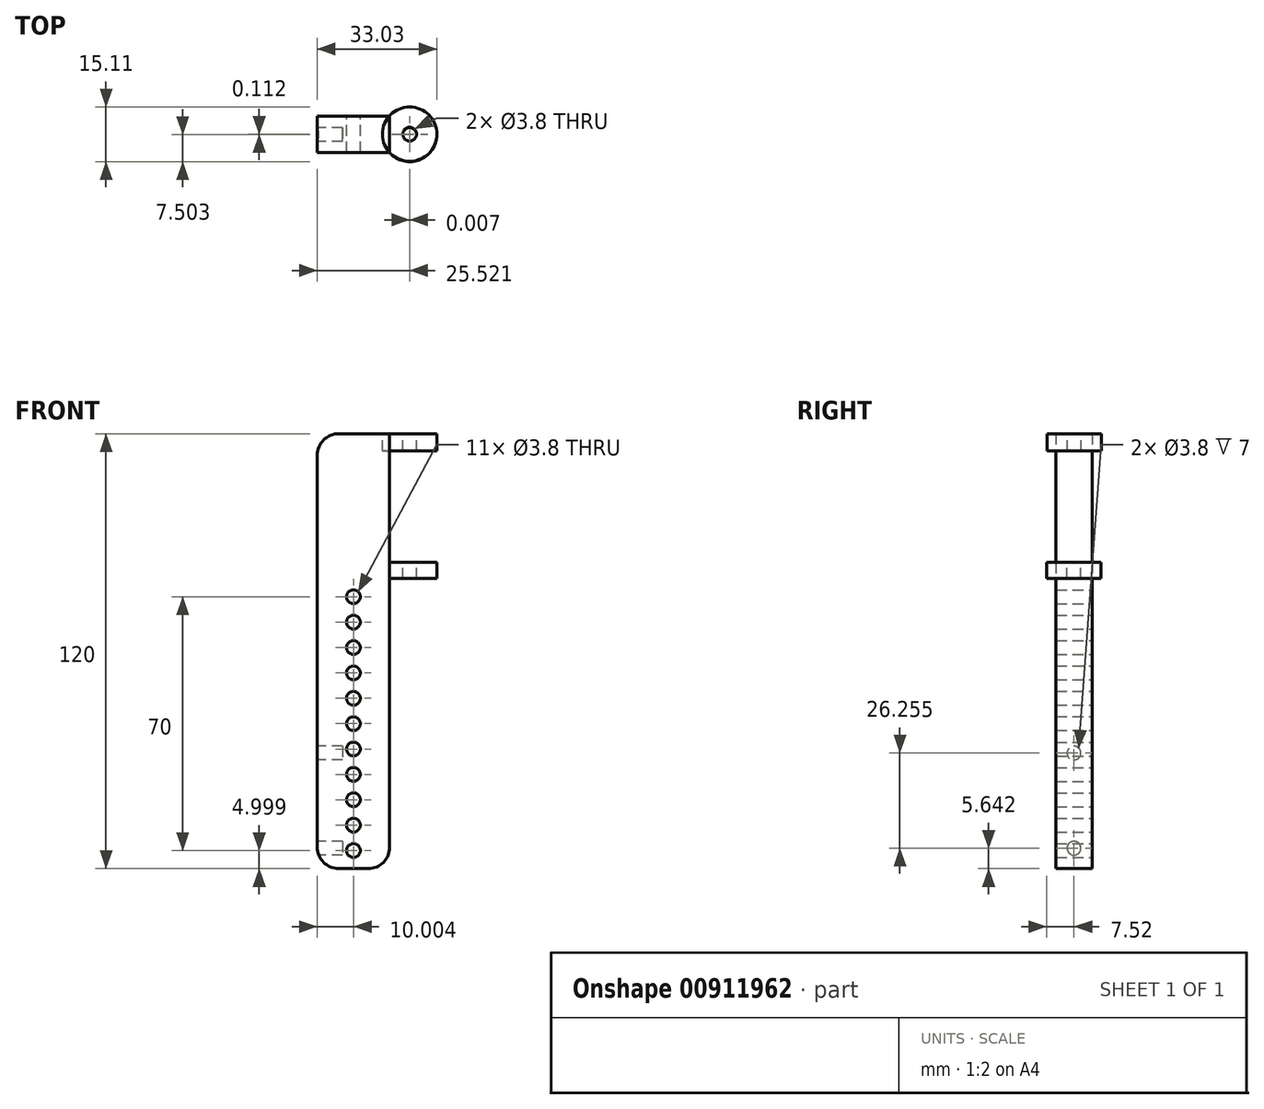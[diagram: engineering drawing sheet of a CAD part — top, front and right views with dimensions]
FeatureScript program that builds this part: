
annotation { "Feature Type Name" : "Feature", "Feature Type Description" : "" }
export const myFeature = defineFeature(function(context is Context, id is Id, definition is map)
    precondition{}
    {
        {
            var Q0;
            Q0=qCreatedBy(makeId("Front.planeOp"),FACE);
            var sketch = newSketch(context, id + "F0", { "sketchPlane" : qUnion([Q0])});
            skLineSegment(sketch, "E0.bottom", {"start": v(-51.22, 126.63) * mm, "end": v(-37.22, 126.63) * mm});
            skLineSegment(sketch, "E0.top", {"start": v(-51.22, 6.63) * mm, "end": v(-43.22, 6.63) * mm});
            skLineSegment(sketch, "E0.left", {"start": v(-57.22, 120.63) * mm, "end": v(-57.22, 12.63) * mm});
            skLineSegment(sketch, "E0.right", {"start": v(-37.22, 126.63) * mm, "end": v(-37.22, 12.63) * mm});
            skPoint(sketch, "E1.visualSharp", {"position": v(-57.22, 126.63) * mm});
            skArc(sketch, "E1.filletArc", {"start": v(-51.22, 126.63) * mm, "mid": v(-55.46, 124.87) * mm, "end": v(-57.22, 120.63) * mm});
            skPoint(sketch, "E2.visualSharp", {"position": v(-57.22, 6.63) * mm});
            skArc(sketch, "E2.filletArc", {"start": v(-57.22, 12.63) * mm, "mid": v(-55.46, 8.39) * mm, "end": v(-51.22, 6.63) * mm});
            skPoint(sketch, "E3.visualSharp", {"position": v(-37.22, 6.63) * mm});
            skArc(sketch, "E3.filletArc", {"start": v(-43.22, 6.63) * mm, "mid": v(-38.97, 8.39) * mm, "end": v(-37.22, 12.63) * mm});
            skSolve(sketch);
        }
        {
            var Q0;
            Q0=qSketchRegion(id+"F0",true);
            extrude(context, id + "F1", {"entities" : qUnion([Q0]), "flatOperationType" : FlatOperationType.REMOVE, "depth" : 10 * mm, "offsetDistance" : 25 * mm, "domain" : OperationDomain.MODEL});
        }
        {
            var Q0;
            Q0=makeQuery(id+"F1.opExtrude","SWEPT_FACE",FACE,{"disambiguationData":[OSD([sQuery(id+"F0.wireOp",EDGE,"E0.bottom")])]});
            var sketch = newSketch(context, id + "F2", { "sketchPlane" : qUnion([Q0])});
            skCircle(sketch, "E4", {"center": v(-31.7, -4.9) * mm, "radius": 7.5 * mm});
            skSolve(sketch);
        }
        {
            var Q0;
            Q0=qSketchRegion(id+"F2",true);
            extrude(context, id + "F3", {"entities" : qUnion([Q0]), "oppositeDirection" : true, "depth" : 4.8 * mm, "offsetDistance" : 25 * mm});
        }
        {
            var Q0;
            Q0=makeQuery(id+"F3.opExtrude","CAP_FACE",FACE,{"disambiguationData":[OSD([sQuery(id+"F2.wireOp",EDGE,"E4")])],"isStart":true});
            var sketch = newSketch(context, id + "F4", { "sketchPlane" : qUnion([Q0])});
            skCircle(sketch, "E5", {"center": v(-31.7, -4.9) * mm, "radius": 1.9 * mm});
            skSolve(sketch);
        }
        {
            var Q0;
            Q0=qSketchRegion(id+"F4",true);
            extrude(context, id + "F5", {"entities" : qUnion([Q0]), "operationType" : NewBodyOperationType.REMOVE, "oppositeDirection" : true, "depth" : 25 * mm, "offsetDistance" : 25 * mm});
        }
        {
            var Q0;
            Q0=makeQuery(id+"F1.opExtrude","SWEPT_FACE",FACE,{"disambiguationData":[OSD([sQuery(id+"F0.wireOp",EDGE,"E0.left")])]});
            var sketch = newSketch(context, id + "F6", { "sketchPlane" : qUnion([Q0])});
            skCircle(sketch, "E6", {"center": v(5, 38.53) * mm, "radius": 1.9 * mm});
            skCircle(sketch, "E7", {"center": v(5, 12.27) * mm, "radius": 1.9 * mm});
            skSolve(sketch);
        }
        {
            var Q0;
            Q0=qSketchRegion(id+"F6",true);
            extrude(context, id + "F7", {"entities" : qUnion([Q0]), "operationType" : NewBodyOperationType.REMOVE, "oppositeDirection" : true, "depth" : 7 * mm, "offsetDistance" : 25 * mm});
        }
        {
            var Q0;
            Q0=makeQuery(id+"F3.opExtrude","CAP_FACE",FACE,{"disambiguationData":[OSD([sQuery(id+"F2.wireOp",EDGE,"E4")])],"isStart":true});
            cPlane(context, id + "F8", {"entities" : qUnion([Q0]), "cplaneType" : CPlaneType.OFFSET, "offset" : 40 * mm, "oppositeDirection" : true, "width" : 150 * mm, "height" : 150 * mm});
        }
        {
            var Q0;
            Q0=qCreatedBy(id+"F8.planeOp",FACE);
            var sketch = newSketch(context, id + "F9", { "sketchPlane" : qUnion([Q0])});
            skCircle(sketch, "E8", {"center": v(-31.7, -5.02) * mm, "radius": 7.5 * mm});
            skSolve(sketch);
        }
        {
            var Q0;
            Q0 = qSketchRegion(id + "F9", true);
            extrude(context, id + "F10", {"entities" : qUnion([Q0]), "operationType" : NewBodyOperationType.ADD, "depth" : 4.5 * mm, "offsetDistance" : 25 * mm});
        }
        {
            var Q0;
            Q0=makeQuery(id+"F10.opExtrude","CAP_FACE",FACE,{"disambiguationData":[OSD([sQuery(id+"F9.wireOp",EDGE,"E8")])],"isStart":false});
            var sketch = newSketch(context, id + "F11", { "sketchPlane" : qUnion([Q0])});
            skCircle(sketch, "E9", {"center": v(-31.7, -5.02) * mm, "radius": 1.9 * mm});
            skSolve(sketch);
        }
        {
            var Q0;
            Q0 = qSketchRegion(id + "F11", true);
            extrude(context, id + "F12", {"entities" : qUnion([Q0]), "operationType" : NewBodyOperationType.REMOVE, "oppositeDirection" : true, "depth" : 25 * mm, "offsetDistance" : 25 * mm});
        }
        {
            var Q0;
            Q0=makeQuery(id+"F1.opExtrude","CAP_FACE",FACE,{"disambiguationData":[OSD([sQuery(id+"F0.wireOp",EDGE,"E0.bottom"),sQuery(id+"F0.wireOp",EDGE,"E0.top"),sQuery(id+"F0.wireOp",EDGE,"E0.left"),sQuery(id+"F0.wireOp",EDGE,"E0.right"),sQuery(id+"F0.wireOp",EDGE,"E1.filletArc"),sQuery(id+"F0.wireOp",EDGE,"E2.filletArc"),sQuery(id+"F0.wireOp",EDGE,"E3.filletArc")])],"isStart":true});
            var sketch = newSketch(context, id + "F13", { "sketchPlane" : qUnion([Q0])});
            skCircle(sketch, "E10", {"center": v(47.22, 81.63) * mm, "radius": 1.9 * mm});
            skCircle(sketch, "E11", {"center": v(47.22, 74.63) * mm, "radius": 1.9 * mm});
            skCircle(sketch, "E12", {"center": v(47.22, 53.63) * mm, "radius": 1.9 * mm});
            skCircle(sketch, "E13", {"center": v(47.22, 67.63) * mm, "radius": 1.9 * mm});
            skCircle(sketch, "E14", {"center": v(47.22, 60.63) * mm, "radius": 1.9 * mm});
            skCircle(sketch, "E15.MirrorC", {"center": v(47.22, 18.63) * mm, "radius": 1.9 * mm});
            skCircle(sketch, "E16.MirrorC", {"center": v(47.22, 25.63) * mm, "radius": 1.9 * mm});
            skCircle(sketch, "E17.MirrorC", {"center": v(47.22, 32.63) * mm, "radius": 1.9 * mm});
            skCircle(sketch, "E18.MirrorC", {"center": v(47.22, 39.63) * mm, "radius": 1.9 * mm});
            skCircle(sketch, "E19.MirrorC", {"center": v(47.22, 46.63) * mm, "radius": 1.9 * mm});
            skCircle(sketch, "E20", {"center": v(47.22, 11.63) * mm, "radius": 1.9 * mm});
            skPoint(sketch, "E21.orphan", {"position": v(47.22, 126.63) * mm});
            skSolve(sketch);
        }
        {
            var Q0;
            Q0 = qSketchRegion(id + "F13", true);
            extrude(context, id + "F14", {"entities" : qUnion([Q0]), "operationType" : NewBodyOperationType.REMOVE, "oppositeDirection" : true, "depth" : 25 * mm, "offsetDistance" : 25 * mm});
        }
    });
